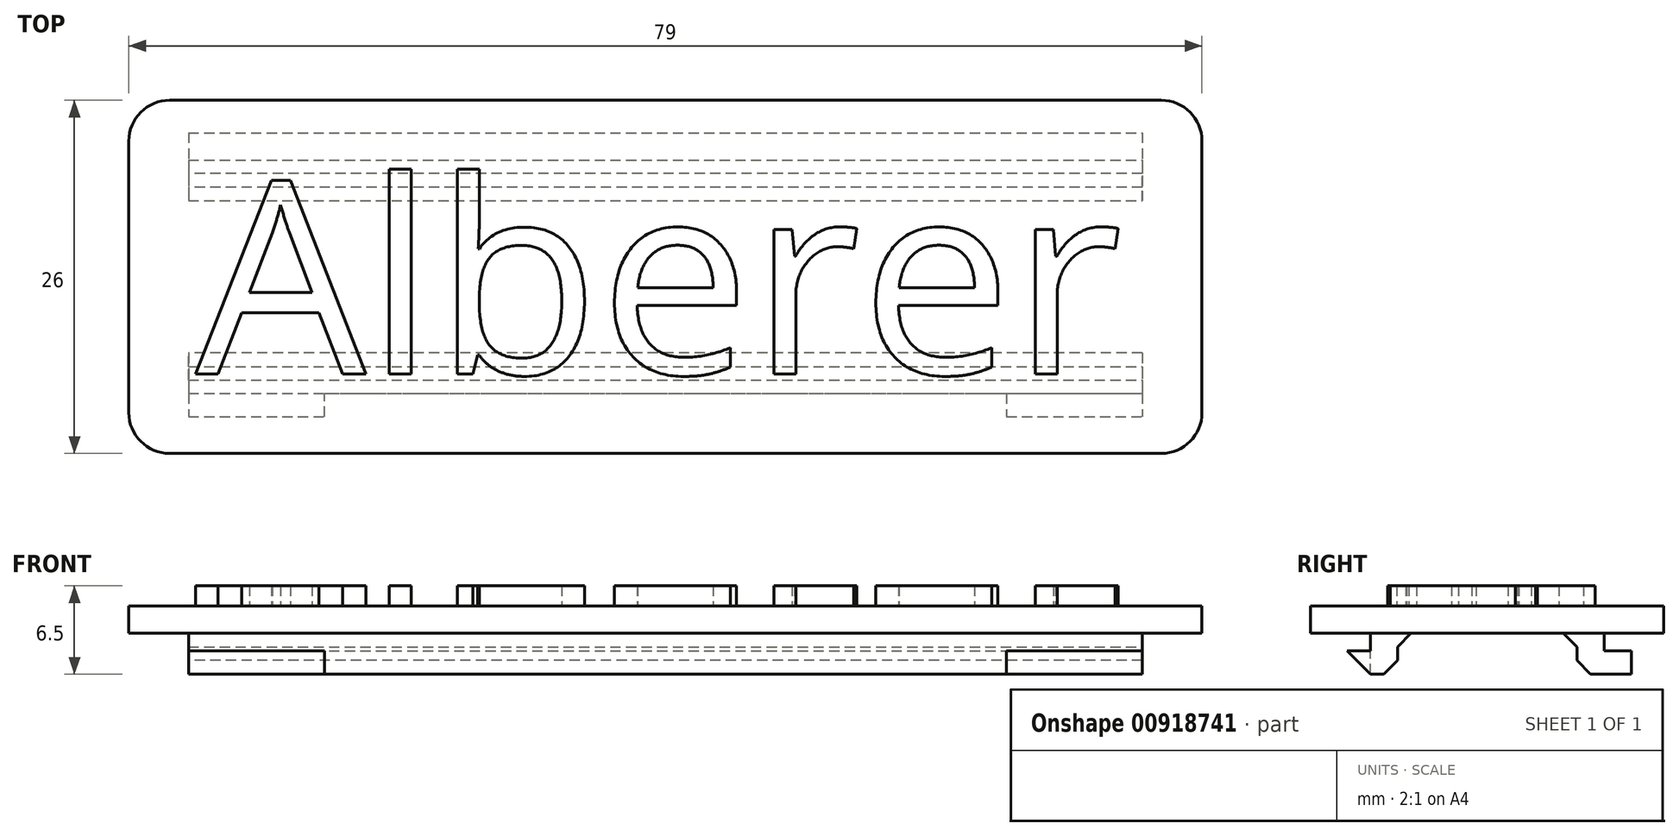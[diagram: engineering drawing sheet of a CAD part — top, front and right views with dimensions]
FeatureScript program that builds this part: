
annotation { "Feature Type Name" : "Feature", "Feature Type Description" : "" }
export const myFeature = defineFeature(function(context is Context, id is Id, definition is map)
    precondition{}
    {
        {
            var Q0;
            Q0=qCreatedBy(makeId("Top.planeOp"),FACE);
            var sketch = newSketch(context, id + "F0", { "sketchPlane" : qUnion([Q0])});
            skLineSegment(sketch, "E0.bottom", {"start": v(39.5, -13) * mm, "end": v(-39.5, -13) * mm});
            skLineSegment(sketch, "E0.top", {"start": v(39.5, 13) * mm, "end": v(-39.5, 13) * mm});
            skLineSegment(sketch, "E0.left", {"start": v(39.5, -13) * mm, "end": v(39.5, 13) * mm});
            skLineSegment(sketch, "E0.right", {"start": v(-39.5, -13) * mm, "end": v(-39.5, 13) * mm});
            skPoint(sketch, "E0.middle", {"position": v(0, 0) * mm});
            skLineSegment(sketch, "E1", {"start": v(-39.5, -8.6) * mm, "end": v(39.5, -8.6) * mm, "construction": true});
            skLineSegment(sketch, "E2.MirrorCS", {"start": v(-39.5, 8.6) * mm, "end": v(39.5, 8.6) * mm, "construction": true});
            skLineSegment(sketch, "E3", {"start": v(-35.1, 8.6) * mm, "end": v(-35.1, -8.6) * mm, "construction": true});
            skLineSegment(sketch, "E4.MirrorCS", {"start": v(35.1, 8.6) * mm, "end": v(35.1, -8.6) * mm, "construction": true});
            skLineSegment(sketch, "E5", {"start": v(-35.1, -8.6) * mm, "end": v(35.1, -8.6) * mm});
            skLineSegment(sketch, "E6", {"start": v(-35.1, -6.6) * mm, "end": v(35.1, -6.6) * mm});
            skLineSegment(sketch, "E7.MirrorCS", {"start": v(-35.1, -10.6) * mm, "end": v(35.1, -10.6) * mm});
            skLineSegment(sketch, "E8.MirrorCS", {"start": v(-35.1, 6.6) * mm, "end": v(35.1, 6.6) * mm});
            skLineSegment(sketch, "E9.MirrorCS", {"start": v(-35.1, 10.6) * mm, "end": v(35.1, 10.6) * mm});
            skLineSegment(sketch, "E10", {"start": v(-35.1, -6.6) * mm, "end": v(-35.1, -10.6) * mm});
            skLineSegment(sketch, "E11", {"start": v(35.1, -6.6) * mm, "end": v(35.1, -10.6) * mm});
            skLineSegment(sketch, "E12", {"start": v(35.1, 10.6) * mm, "end": v(35.1, 6.6) * mm});
            skLineSegment(sketch, "E13", {"start": v(-35.1, 10.6) * mm, "end": v(-35.1, 6.6) * mm});
            skLineSegment(sketch, "E14.MirrorCS", {"start": v(-35.1, 8.6) * mm, "end": v(35.1, 8.6) * mm});
            skLineSegment(sketch, "E15", {"start": v(-25.1, -6.6) * mm, "end": v(-25.1, -10.6) * mm});
            skLineSegment(sketch, "E16.MirrorCS", {"start": v(25.1, -6.6) * mm, "end": v(25.1, -10.6) * mm});
            skSolve(sketch);
        }
        {
            var Q0;
            {var subQ0=sQuery(id+"F0.wireOp",EDGE,"E5");Q0=makeQuery(id+"F0.imprint","IMPRINT",FACE,{"disambiguationData":[TD([[makeQuery(id+"F0.imprint","IMPRINT",EDGE,{"derivedFrom":subQ0}),1.0]])]});}
            var Q1;
            {var subQ0=sQuery(id+"F0.wireOp",EDGE,"E5");Q1=makeQuery(id+"F0.imprint","IMPRINT",FACE,{"disambiguationData":[TD([[makeQuery(id+"F0.imprint","IMPRINT",EDGE,{"derivedFrom":subQ0}),-1.0]])]});}
            var Q2;
            {var subQ0=sQuery(id+"F0.wireOp",EDGE,"E8.MirrorCS");Q2=makeQuery(id+"F0.imprint","IMPRINT",FACE,{"disambiguationData":[TD([[makeQuery(id+"F0.imprint","IMPRINT",EDGE,{"derivedFrom":subQ0}),1.0]])]});}
            var Q3;
            {var subQ0=sQuery(id+"F0.wireOp",EDGE,"E9.MirrorCS");Q3=makeQuery(id+"F0.imprint","IMPRINT",FACE,{"disambiguationData":[TD([[makeQuery(id+"F0.imprint","IMPRINT",EDGE,{"derivedFrom":subQ0}),-1.0]])]});}
            var Q4;
            Q4=makeQuery(id+"F0.imprint","IMPRINT",FACE,{"disambiguationData":[TD([[makeQuery(id+"F0.imprint","IMPRINT",EDGE,{"derivedFrom":sQuery(id+"F0.wireOp",EDGE,"E0.bottom")}),-1.0]])]});
            extrude(context, id + "F1", {"entities" : qUnion([Q0, Q1, Q2, Q3, Q4]), "depth" : -2 * mm, "offsetDistance" : 25 * mm});
        }
        {
            var Q0;
            {var subQ0=sQuery(id+"F0.wireOp",EDGE,"E10");var subQ1=sQuery(id+"F0.wireOp",EDGE,"E5");var subQ2=makeQuery(id+"F0.imprint","INTERSECT",VERTEX,{"derivedFrom":[subQ1,subQ0]});Q0=makeQuery(id+"F0.imprint","IMPRINT",FACE,{"disambiguationData":[TD([[makeQuery(id+"F0.imprint","IMPRINT",EDGE,{"disambiguationData":[TD([[subQ2,-1.0]])],"derivedFrom":subQ1}),1.0]])]});}
            var Q1;
            {var subQ0=sQuery(id+"F0.wireOp",EDGE,"E11");var subQ1=sQuery(id+"F0.wireOp",EDGE,"E5");var subQ2=makeQuery(id+"F0.imprint","INTERSECT",VERTEX,{"derivedFrom":[subQ1,subQ0]});Q1=makeQuery(id+"F0.imprint","IMPRINT",FACE,{"disambiguationData":[TD([[makeQuery(id+"F0.imprint","IMPRINT",EDGE,{"disambiguationData":[TD([[subQ2,1.0]])],"derivedFrom":subQ1}),1.0]])]});}
            var Q2;
            {var subQ0=sQuery(id+"F0.wireOp",EDGE,"E8.MirrorCS");Q2=makeQuery(id+"F0.imprint","IMPRINT",FACE,{"disambiguationData":[TD([[makeQuery(id+"F0.imprint","IMPRINT",EDGE,{"derivedFrom":subQ0}),1.0]])]});}
            var Q3;
            {var subQ0=sQuery(id+"F0.wireOp",EDGE,"E10");var subQ1=sQuery(id+"F0.wireOp",EDGE,"E5");var subQ2=makeQuery(id+"F0.imprint","INTERSECT",VERTEX,{"derivedFrom":[subQ1,subQ0]});Q3=makeQuery(id+"F0.imprint","IMPRINT",FACE,{"disambiguationData":[TD([[makeQuery(id+"F0.imprint","IMPRINT",EDGE,{"disambiguationData":[TD([[subQ2,-1.0]])],"derivedFrom":subQ1}),-1.0]])]});}
            var Q4;
            {var subQ0=sQuery(id+"F0.wireOp",EDGE,"E11");var subQ1=sQuery(id+"F0.wireOp",EDGE,"E5");var subQ2=makeQuery(id+"F0.imprint","INTERSECT",VERTEX,{"derivedFrom":[subQ1,subQ0]});Q4=makeQuery(id+"F0.imprint","IMPRINT",FACE,{"disambiguationData":[TD([[makeQuery(id+"F0.imprint","IMPRINT",EDGE,{"disambiguationData":[TD([[subQ2,1.0]])],"derivedFrom":subQ1}),-1.0]])]});}
            var Q5;
            {var subQ0=sQuery(id+"F0.wireOp",EDGE,"E9.MirrorCS");Q5=makeQuery(id+"F0.imprint","IMPRINT",FACE,{"disambiguationData":[TD([[makeQuery(id+"F0.imprint","IMPRINT",EDGE,{"derivedFrom":subQ0}),-1.0]])]});}
            var Q6;
            {var subQ0=sQuery(id+"F0.wireOp",EDGE,"E15");var subQ1=sQuery(id+"F0.wireOp",EDGE,"E5");var subQ2=makeQuery(id+"F0.imprint","INTERSECT",VERTEX,{"derivedFrom":[subQ1,subQ0]});Q6=makeQuery(id+"F0.imprint","IMPRINT",FACE,{"disambiguationData":[TD([[makeQuery(id+"F0.imprint","IMPRINT",EDGE,{"disambiguationData":[TD([[subQ2,-1.0]])],"derivedFrom":subQ1}),1.0]])]});}
            extrude(context, id + "F2", {"entities" : qUnion([Q0, Q1, Q2, Q3, Q4, Q5, Q6]), "operationType" : NewBodyOperationType.ADD, "depth" : -5 * mm, "offsetDistance" : 25 * mm});
        }
        {
            var Q0;
            {var subQ0=sQuery(id+"F0.wireOp",EDGE,"E5");Q0=makeQuery(id+"F0.imprint","IMPRINT",FACE,{"disambiguationData":[TD([[makeQuery(id+"F0.imprint","IMPRINT",EDGE,{"derivedFrom":subQ0}),-1.0]])]});}
            var Q1;
            {var subQ0=sQuery(id+"F0.wireOp",EDGE,"E9.MirrorCS");Q1=makeQuery(id+"F0.imprint","IMPRINT",FACE,{"disambiguationData":[TD([[makeQuery(id+"F0.imprint","IMPRINT",EDGE,{"derivedFrom":subQ0}),-1.0]])]});}
            extrude(context, id + "F3", {"entities" : qUnion([Q0, Q1]), "operationType" : NewBodyOperationType.REMOVE, "depth" : -3.3 * mm, "offsetDistance" : 25 * mm, "hasSecondDirection" : true, "secondDirectionOppositeDirection" : false, "secondDirectionDepth" : -2 * mm});
        }
        {
            var Q0;
            Q0=makeQuery(id+"F3.boolean.opBoolean","COPY",EDGE,{"derivedFrom":makeQuery(id+"F3.opExtrude","CAP_EDGE",EDGE,{"disambiguationData":[OSD([sQuery(id+"F0.wireOp",EDGE,"E9.MirrorCS")])],"isStart":false})});
            var Q1;
            Q1=makeQuery(id+"F2.opExtrude","CAP_EDGE",EDGE,{"disambiguationData":[OSD([sQuery(id+"F0.wireOp",EDGE,"E8.MirrorCS")])],"isStart":false});
            var Q2;
            Q2=makeQuery(id+"F2.boolean.opBoolean","INTERSECT",EDGE,{"derivedFrom":[makeQuery(id+"F1.opExtrude","CAP_FACE",FACE,{"disambiguationData":[OSD([sQuery(id+"F0.wireOp",EDGE,"E0.bottom"),sQuery(id+"F0.wireOp",EDGE,"E0.top"),sQuery(id+"F0.wireOp",EDGE,"E0.left"),sQuery(id+"F0.wireOp",EDGE,"E0.right")])],"isStart":false}),makeQuery(id+"F2.opExtrude","SWEPT_FACE",FACE,{"disambiguationData":[OSD([sQuery(id+"F0.wireOp",EDGE,"E8.MirrorCS")])]})]});
            var Q3;
            Q3=makeQuery(id+"F2.boolean.opBoolean","INTERSECT",EDGE,{"derivedFrom":[makeQuery(id+"F1.opExtrude","CAP_FACE",FACE,{"disambiguationData":[OSD([sQuery(id+"F0.wireOp",EDGE,"E0.bottom"),sQuery(id+"F0.wireOp",EDGE,"E0.top"),sQuery(id+"F0.wireOp",EDGE,"E0.left"),sQuery(id+"F0.wireOp",EDGE,"E0.right")])],"isStart":false}),makeQuery(id+"F2.opExtrude","SWEPT_FACE",FACE,{"disambiguationData":[OSD([sQuery(id+"F0.wireOp",EDGE,"E6")])]})]});
            var Q4;
            Q4=makeQuery(id+"F2.opExtrude","CAP_EDGE",EDGE,{"disambiguationData":[OSD([sQuery(id+"F0.wireOp",EDGE,"E6")])],"isStart":false});
            chamfer(context, id + "F4", {"entities" : qUnion([Q0, Q1, Q2, Q3, Q4]), "width" : 1 * mm, "tangentPropagation" : true});
        }
        {
            var Q0;
            Q0=makeQuery(id+"F2.opExtrude","CAP_EDGE",EDGE,{"disambiguationData":[OSD([sQuery(id+"F0.wireOp",EDGE,"E7.MirrorCS")])],"isStart":false});
            chamfer(context, id + "F5", {"entities" : qUnion([Q0]), "chamferType" : ChamferType.TWO_OFFSETS, "width1" : 2 * mm, "oppositeDirection" : false, "width2" : 2 * mm, "tangentPropagation" : true});
        }
        {
            var Q0;
            Q0=makeQuery(id+"F0.imprint","IMPRINT",FACE,{"disambiguationData":[TD([[makeQuery(id+"F0.imprint","IMPRINT",EDGE,{"derivedFrom":sQuery(id+"F0.wireOp",EDGE,"E0.bottom")}),-1.0]])]});
            var sketch = newSketch(context, id + "F6", { "sketchPlane" : qUnion([Q0])});
            skText(sketch, "E17", { "text": "Alberer", "fontName": "OpenSans-Regular.ttf"});
            skPoint(sketch, "E18", {"position": v(0, 0) * mm});
            const initialGuessF6  = {"E17": [-0.0346, -0.00714, 1, 0, 0.01429]};
            skSetInitialGuess(sketch, initialGuessF6);
            skSolve(sketch);
        }
        {
            var Q0;
            Q0 = qSketchRegion(id + "F6", true);
            extrude(context, id + "F7", {"entities" : qUnion([Q0]), "operationType" : NewBodyOperationType.ADD, "depth" : 1.5 * mm, "offsetDistance" : 25 * mm});
        }
        {
            var Q0;
            Q0=makeQuery(id+"F1.opExtrude","SWEPT_EDGE",EDGE,{"disambiguationData":[OSD([sQuery(id+"F0.wireOp",EDGE,"E0.top"),sQuery(id+"F0.wireOp",EDGE,"E0.left")])]});
            var Q1;
            Q1=makeQuery(id+"F1.opExtrude","SWEPT_EDGE",EDGE,{"disambiguationData":[OSD([sQuery(id+"F0.wireOp",EDGE,"E0.top"),sQuery(id+"F0.wireOp",EDGE,"E0.right")])]});
            var Q2;
            Q2=makeQuery(id+"F1.opExtrude","SWEPT_EDGE",EDGE,{"disambiguationData":[OSD([sQuery(id+"F0.wireOp",EDGE,"E0.bottom"),sQuery(id+"F0.wireOp",EDGE,"E0.right")])]});
            var Q3;
            Q3=makeQuery(id+"F1.opExtrude","SWEPT_EDGE",EDGE,{"disambiguationData":[OSD([sQuery(id+"F0.wireOp",EDGE,"E0.bottom"),sQuery(id+"F0.wireOp",EDGE,"E0.left")])]});
            fillet(context, id + "F8", {"entities" : qUnion([Q0, Q1, Q2, Q3]), "radius" : 3 * mm, "tangentPropagation" : true, "allowEdgeOverflow" : false});
        }
    });
